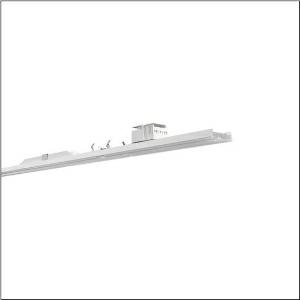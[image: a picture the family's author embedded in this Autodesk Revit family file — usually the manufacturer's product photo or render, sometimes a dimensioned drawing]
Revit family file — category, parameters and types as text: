
# Revit family: licross_r__11_recessed_tw_51tl12tnt8xw_1b1b
name_source: partatom
category: Lighting Fixtures
units: mm (PartAtom-declared; Revit-internal decimal feet)

## family parameters
Cut with Voids When Loaded = No
Host = Face
Light Source = No
Part Type = Normal
Room Calculation Point = No
Round Connector Dimension = Use Diameter
Shared = No

## types (1)
- --- (1 x LED 2700 K ... 6500 K, 8460 lm, 57.4 W, 2700K)
    Apparent Load = 57 VA
    CIE Flux Codes = 66 91 98 100 100
    Color Rendering = 80
    Color Temperature = 2700K
    Default Elevation = 1800 mm
    Description = Licross® 11 Recessed TWluminaire insert, length: 1.500mm, width: 66mm, height: 67mm, LED rated luminous flux: 8.460lm, light colour: 8tw, control gear: DALI DT8, control gear: ECG DALI, with plug, 5-pole, with phase selection, mains connection: 220..240V, AC, 50/60Hz, halogen-free wiring, primary optical cover: cover, of PMMA, light emission: direct distribution, protection rating (complete): IP40, insulation class (complete): insulation class I (protective earthing), certification: CE, ENEC, VDE, protection symbol: D if used in an environment without relevant dust loads with corresponding accessories, permissible ambient temperature for indoor applications: -25..+35°C, reducing of maximum allowable ambient temperature of 5°C with ceiling mounting, corresponds to IFS (International Featured Standards) requirements for safety and quality in the food industry, packaging unit: 1 piece
    Height = 58 mm
    Lamp = 1 x LED 2700 K ... 6500 K
    Lamp Light Flux = 8460 lm
    Lamp Power = 57.4 W
    Lamp count = 1
    Length = 1500 mm
    Luminous efficacy = 147 lm/W
    Manufacturer = Siteco
    ModVariant = No
    Model = 51TL12TNT8XW
    Mounting Place = Ceiling
    Mounting Type = Pendant
    Number of Poles = 1
    OnlyDefault = Yes
    Power Factor = 1
    Product Name = Licross® 11 Recessed TW
    Product group = luminaire insert
    ProductGroupID = 902
    Protection Class = Protection class I
    Protection Degree = IP 40
    RLX_Detail_Level = 1
    RlxData = <blob elided: 18685 chars, md5=4641299c>
    Socket = socket
    Standby Power = 0 W
    System Light Flux = 8460 lm
    System Power = 57 W
    Type Comments = individual setting: CCT=2700K
    Type Image = l_1266722.jpg
    URL = http://relux.com
    VarID = @adj_138845
    Voltage = 0 V
    Weight = 0.00 kg
    Width = 66 mm

## geometry (parser evidence)
native form markers: Blend x4, Sweep x10
no freeform markers — native parametric forms only
